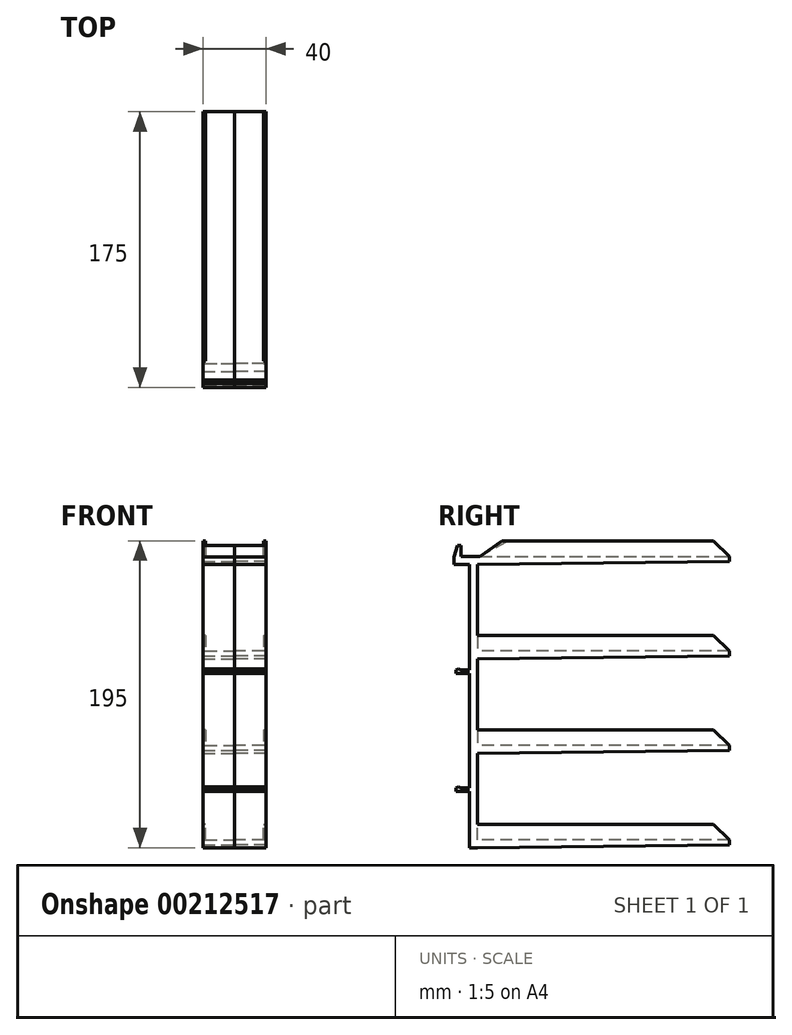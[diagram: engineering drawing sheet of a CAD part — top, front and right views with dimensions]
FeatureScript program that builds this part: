
annotation { "Feature Type Name" : "Feature", "Feature Type Description" : "" }
export const myFeature = defineFeature(function(context is Context, id is Id, definition is map)
    precondition{}
    {
        {
            var Q0;
            Q0=qCreatedBy(makeId("Right.planeOp"),FACE);
            var sketch = newSketch(context, id + "F0", { "sketchPlane" : qUnion([Q0])});
            skLineSegment(sketch, "E0", {"start": v(0, 0) * mm, "end": v(0, 67) * mm});
            skLineSegment(sketch, "E1", {"start": v(0, 67) * mm, "end": v(-10, 67) * mm});
            skLineSegment(sketch, "E2", {"start": v(-10, 67) * mm, "end": v(-10, 79) * mm});
            skLineSegment(sketch, "E3", {"start": v(-10, 79) * mm, "end": v(-5.5, 79) * mm});
            skLineSegment(sketch, "E4", {"start": v(-5.5, 79) * mm, "end": v(-5.5, 72) * mm});
            skLineSegment(sketch, "E5", {"start": v(-5.5, 72) * mm, "end": v(5, 72) * mm});
            skLineSegment(sketch, "E6", {"start": v(0, 0) * mm, "end": v(-5.5, 0) * mm});
            skLineSegment(sketch, "E7", {"start": v(-5.5, 0) * mm, "end": v(-5.5, 0.75) * mm});
            skLineSegment(sketch, "E8", {"start": v(-5.5, 0.75) * mm, "end": v(-8.5, 0.75) * mm});
            skLineSegment(sketch, "E9", {"start": v(-8.5, 0.75) * mm, "end": v(-8.5, -2.25) * mm});
            skLineSegment(sketch, "E10", {"start": v(-8.5, -2.25) * mm, "end": v(0, -2.25) * mm});
            skLineSegment(sketch, "E11", {"start": v(0, -2.25) * mm, "end": v(0, -58.03) * mm});
            skLineSegment(sketch, "E12", {"start": v(0, 0) * mm, "end": v(27.42, 0) * mm, "construction": true});
            skLineSegment(sketch, "E13", {"start": v(27.42, 0) * mm, "end": v(27.42, -75) * mm, "construction": true});
            skLineSegment(sketch, "E14", {"start": v(27.42, -75) * mm, "end": v(0, -75) * mm, "construction": true});
            skLineSegment(sketch, "E15", {"start": v(0, -58.03) * mm, "end": v(0, -75) * mm});
            skLineSegment(sketch, "E16", {"start": v(0, -75) * mm, "end": v(-5.5, -75) * mm});
            skLineSegment(sketch, "E17", {"start": v(-5.5, -75) * mm, "end": v(-5.5, -74.25) * mm});
            skLineSegment(sketch, "E18", {"start": v(-5.5, -74.25) * mm, "end": v(-8.5, -74.25) * mm});
            skLineSegment(sketch, "E19", {"start": v(-8.5, -74.25) * mm, "end": v(-8.5, -77.25) * mm});
            skLineSegment(sketch, "E20", {"start": v(-8.5, -77.25) * mm, "end": v(0, -77.25) * mm});
            skLineSegment(sketch, "E21", {"start": v(5, 72) * mm, "end": v(165, 72) * mm});
            skLineSegment(sketch, "E22", {"start": v(165, 72) * mm, "end": v(165, 69) * mm});
            skLineSegment(sketch, "E23", {"start": v(165, 72) * mm, "end": v(165, 12) * mm, "construction": true});
            skLineSegment(sketch, "E24", {"start": v(165, 12) * mm, "end": v(165, -48) * mm, "construction": true});
            skLineSegment(sketch, "E25", {"start": v(165, -48) * mm, "end": v(165, -108) * mm, "construction": true});
            skLineSegment(sketch, "E26", {"start": v(165, -108) * mm, "end": v(5, -108) * mm});
            skLineSegment(sketch, "E27", {"start": v(165, -108) * mm, "end": v(165, -111) * mm});
            skLineSegment(sketch, "E28", {"start": v(165, -111) * mm, "end": v(5, -113) * mm});
            skLineSegment(sketch, "E29", {"start": v(0, -77.25) * mm, "end": v(0, -113) * mm});
            skLineSegment(sketch, "E30", {"start": v(5, -113) * mm, "end": v(0, -113) * mm});
            skLineSegment(sketch, "E31", {"start": v(165, -48) * mm, "end": v(5, -48) * mm});
            skLineSegment(sketch, "E32", {"start": v(165, 12) * mm, "end": v(5, 12) * mm});
            skLineSegment(sketch, "E33", {"start": v(165, 12) * mm, "end": v(165, 9) * mm});
            skLineSegment(sketch, "E34", {"start": v(165, 9) * mm, "end": v(5, 7) * mm});
            skLineSegment(sketch, "E35", {"start": v(165, -48) * mm, "end": v(165, -51) * mm});
            skLineSegment(sketch, "E36", {"start": v(165, -51) * mm, "end": v(5, -53) * mm});
            skLineSegment(sketch, "E37", {"start": v(5, 72) * mm, "end": v(5, 67) * mm, "construction": true});
            skLineSegment(sketch, "E38", {"start": v(5, 67) * mm, "end": v(165, 69) * mm});
            skLineSegment(sketch, "E39", {"start": v(5, 67) * mm, "end": v(5, 12) * mm});
            skLineSegment(sketch, "E40", {"start": v(5, 7) * mm, "end": v(5, -48) * mm});
            skLineSegment(sketch, "E41", {"start": v(5, -108) * mm, "end": v(5, -53) * mm});
            skSolve(sketch);
        }
        {
            var Q0;
            Q0=makeQuery(id+"F0.imprint","IMPRINT",FACE,{"disambiguationData":[TD([[makeQuery(id+"F0.imprint","IMPRINT",EDGE,{"derivedFrom":sQuery(id+"F0.wireOp",EDGE,"E0")}),-1.0]])]});
            extrude(context, id + "F1", {"entities" : qUnion([Q0]), "depth" : 20 * mm});
        }
        {
            var Q0;
            Q0=makeQuery(id+"F1.opExtrude","CAP_FACE",FACE,{"disambiguationData":[OSD([sQuery(id+"F0.wireOp",EDGE,"E0"),sQuery(id+"F0.wireOp",EDGE,"E1"),sQuery(id+"F0.wireOp",EDGE,"E2"),sQuery(id+"F0.wireOp",EDGE,"E3"),sQuery(id+"F0.wireOp",EDGE,"E4"),sQuery(id+"F0.wireOp",EDGE,"E5"),sQuery(id+"F0.wireOp",EDGE,"E6"),sQuery(id+"F0.wireOp",EDGE,"E7"),sQuery(id+"F0.wireOp",EDGE,"E8"),sQuery(id+"F0.wireOp",EDGE,"E9"),sQuery(id+"F0.wireOp",EDGE,"E10"),sQuery(id+"F0.wireOp",EDGE,"E11"),sQuery(id+"F0.wireOp",EDGE,"E15"),sQuery(id+"F0.wireOp",EDGE,"E16"),sQuery(id+"F0.wireOp",EDGE,"E17"),sQuery(id+"F0.wireOp",EDGE,"E18"),sQuery(id+"F0.wireOp",EDGE,"E19"),sQuery(id+"F0.wireOp",EDGE,"E20"),sQuery(id+"F0.wireOp",EDGE,"E21"),sQuery(id+"F0.wireOp",EDGE,"E22"),sQuery(id+"F0.wireOp",EDGE,"E26"),sQuery(id+"F0.wireOp",EDGE,"E27"),sQuery(id+"F0.wireOp",EDGE,"E28"),sQuery(id+"F0.wireOp",EDGE,"E29"),sQuery(id+"F0.wireOp",EDGE,"E30"),sQuery(id+"F0.wireOp",EDGE,"E31"),sQuery(id+"F0.wireOp",EDGE,"E32"),sQuery(id+"F0.wireOp",EDGE,"E33"),sQuery(id+"F0.wireOp",EDGE,"E34"),sQuery(id+"F0.wireOp",EDGE,"E35"),sQuery(id+"F0.wireOp",EDGE,"E36"),sQuery(id+"F0.wireOp",EDGE,"E38"),sQuery(id+"F0.wireOp",EDGE,"E39"),sQuery(id+"F0.wireOp",EDGE,"E40"),sQuery(id+"F0.wireOp",EDGE,"E41")])],"isStart":false});
            var sketch = newSketch(context, id + "F2", { "sketchPlane" : qUnion([Q0])});
            skLineSegment(sketch, "E42", {"start": v(-7.75, 79) * mm, "end": v(-10, 71.88) * mm});
            skLineSegment(sketch, "E43", {"start": v(-10, 71.88) * mm, "end": v(-10, 79) * mm});
            skLineSegment(sketch, "E44", {"start": v(-10, 79) * mm, "end": v(-7.75, 79) * mm});
            skSolve(sketch);
        }
        {
            var Q0;
            Q0=makeQuery(id+"F2.imprint","IMPRINT",FACE,{"disambiguationData":[TD([[makeQuery(id+"F2.imprint","IMPRINT",EDGE,{"derivedFrom":sQuery(id+"F2.wireOp",EDGE,"E42")}),-1.0]])]});
            extrude(context, id + "F3", {"entities" : qUnion([Q0]), "operationType" : NewBodyOperationType.REMOVE, "endBound" : BoundingType.UP_TO_NEXT, "oppositeDirection" : true, "depth" : 10 * mm});
        }
        {
            var Q0;
            Q0=makeQuery(id+"F1.opExtrude","CAP_FACE",FACE,{"disambiguationData":[OSD([sQuery(id+"F0.wireOp",EDGE,"E0"),sQuery(id+"F0.wireOp",EDGE,"E1"),sQuery(id+"F0.wireOp",EDGE,"E2"),sQuery(id+"F0.wireOp",EDGE,"E3"),sQuery(id+"F0.wireOp",EDGE,"E4"),sQuery(id+"F0.wireOp",EDGE,"E5"),sQuery(id+"F0.wireOp",EDGE,"E6"),sQuery(id+"F0.wireOp",EDGE,"E7"),sQuery(id+"F0.wireOp",EDGE,"E8"),sQuery(id+"F0.wireOp",EDGE,"E9"),sQuery(id+"F0.wireOp",EDGE,"E10"),sQuery(id+"F0.wireOp",EDGE,"E11"),sQuery(id+"F0.wireOp",EDGE,"E15"),sQuery(id+"F0.wireOp",EDGE,"E16"),sQuery(id+"F0.wireOp",EDGE,"E17"),sQuery(id+"F0.wireOp",EDGE,"E18"),sQuery(id+"F0.wireOp",EDGE,"E19"),sQuery(id+"F0.wireOp",EDGE,"E20"),sQuery(id+"F0.wireOp",EDGE,"E21"),sQuery(id+"F0.wireOp",EDGE,"E22"),sQuery(id+"F0.wireOp",EDGE,"E26"),sQuery(id+"F0.wireOp",EDGE,"E27"),sQuery(id+"F0.wireOp",EDGE,"E28"),sQuery(id+"F0.wireOp",EDGE,"E29"),sQuery(id+"F0.wireOp",EDGE,"E30"),sQuery(id+"F0.wireOp",EDGE,"E31"),sQuery(id+"F0.wireOp",EDGE,"E32"),sQuery(id+"F0.wireOp",EDGE,"E33"),sQuery(id+"F0.wireOp",EDGE,"E34"),sQuery(id+"F0.wireOp",EDGE,"E35"),sQuery(id+"F0.wireOp",EDGE,"E36"),sQuery(id+"F0.wireOp",EDGE,"E38"),sQuery(id+"F0.wireOp",EDGE,"E39"),sQuery(id+"F0.wireOp",EDGE,"E40"),sQuery(id+"F0.wireOp",EDGE,"E41")])],"isStart":false});
            var sketch = newSketch(context, id + "F4", { "sketchPlane" : qUnion([Q0])});
            skLineSegment(sketch, "E45", {"start": v(-5.5, 0) * mm, "end": v(-7, 0.75) * mm});
            skLineSegment(sketch, "E46", {"start": v(-7, 0.75) * mm, "end": v(-8.5, 0) * mm});
            skLineSegment(sketch, "E47", {"start": v(-8.5, 0) * mm, "end": v(-8.5, 0.75) * mm});
            skLineSegment(sketch, "E48", {"start": v(-8.5, 0.75) * mm, "end": v(-7, 0.75) * mm});
            skLineSegment(sketch, "E49", {"start": v(-5.5, 0.75) * mm, "end": v(-5.5, 0) * mm});
            skSolve(sketch);
        }
        {
            var Q0;
            Q0=makeQuery(id+"F4.imprint","IMPRINT",FACE,{"disambiguationData":[TD([[makeQuery(id+"F4.imprint","IMPRINT",EDGE,{"derivedFrom":sQuery(id+"F4.wireOp",EDGE,"E46")}),-1.0]])]});
            var Q1;
            {var subQ0=sQuery(id+"F4.wireOp",EDGE,"E45");Q1=makeQuery(id+"F4.imprint","IMPRINT",FACE,{"disambiguationData":[TD([[makeQuery(id+"F4.imprint","IMPRINT",EDGE,{"derivedFrom":subQ0}),-1.0]])]});}
            extrude(context, id + "F5", {"entities" : qUnion([Q0, Q1]), "operationType" : NewBodyOperationType.REMOVE, "endBound" : BoundingType.UP_TO_NEXT, "oppositeDirection" : true, "depth" : 10 * mm});
        }
        {
            var Q0;
            Q0=makeQuery(id+"F1.opExtrude","CAP_FACE",FACE,{"disambiguationData":[OSD([sQuery(id+"F0.wireOp",EDGE,"E0"),sQuery(id+"F0.wireOp",EDGE,"E1"),sQuery(id+"F0.wireOp",EDGE,"E2"),sQuery(id+"F0.wireOp",EDGE,"E3"),sQuery(id+"F0.wireOp",EDGE,"E4"),sQuery(id+"F0.wireOp",EDGE,"E5"),sQuery(id+"F0.wireOp",EDGE,"E6"),sQuery(id+"F0.wireOp",EDGE,"E7"),sQuery(id+"F0.wireOp",EDGE,"E8"),sQuery(id+"F0.wireOp",EDGE,"E9"),sQuery(id+"F0.wireOp",EDGE,"E10"),sQuery(id+"F0.wireOp",EDGE,"E11"),sQuery(id+"F0.wireOp",EDGE,"E15"),sQuery(id+"F0.wireOp",EDGE,"E16"),sQuery(id+"F0.wireOp",EDGE,"E17"),sQuery(id+"F0.wireOp",EDGE,"E18"),sQuery(id+"F0.wireOp",EDGE,"E19"),sQuery(id+"F0.wireOp",EDGE,"E20"),sQuery(id+"F0.wireOp",EDGE,"E21"),sQuery(id+"F0.wireOp",EDGE,"E22"),sQuery(id+"F0.wireOp",EDGE,"E26"),sQuery(id+"F0.wireOp",EDGE,"E27"),sQuery(id+"F0.wireOp",EDGE,"E28"),sQuery(id+"F0.wireOp",EDGE,"E29"),sQuery(id+"F0.wireOp",EDGE,"E30"),sQuery(id+"F0.wireOp",EDGE,"E31"),sQuery(id+"F0.wireOp",EDGE,"E32"),sQuery(id+"F0.wireOp",EDGE,"E33"),sQuery(id+"F0.wireOp",EDGE,"E34"),sQuery(id+"F0.wireOp",EDGE,"E35"),sQuery(id+"F0.wireOp",EDGE,"E36"),sQuery(id+"F0.wireOp",EDGE,"E38"),sQuery(id+"F0.wireOp",EDGE,"E39"),sQuery(id+"F0.wireOp",EDGE,"E40"),sQuery(id+"F0.wireOp",EDGE,"E41")])],"isStart":false});
            var sketch = newSketch(context, id + "F6", { "sketchPlane" : qUnion([Q0])});
            skLineSegment(sketch, "E50", {"start": v(-5.5, -75) * mm, "end": v(-7, -74.25) * mm});
            skLineSegment(sketch, "E51", {"start": v(-7, -74.25) * mm, "end": v(-8.5, -75) * mm});
            skLineSegment(sketch, "E52", {"start": v(-8.5, -75) * mm, "end": v(-8.5, -74.25) * mm});
            skLineSegment(sketch, "E53", {"start": v(-8.5, -74.25) * mm, "end": v(-7, -74.25) * mm});
            skLineSegment(sketch, "E54", {"start": v(-5.5, -74.25) * mm, "end": v(-5.5, -75) * mm});
            skSolve(sketch);
        }
        {
            var Q0;
            Q0=makeQuery(id+"F6.imprint","IMPRINT",FACE,{"disambiguationData":[TD([[makeQuery(id+"F6.imprint","IMPRINT",EDGE,{"derivedFrom":sQuery(id+"F6.wireOp",EDGE,"E51")}),-1.0]])]});
            var Q1;
            {var subQ0=sQuery(id+"F6.wireOp",EDGE,"E50");Q1=makeQuery(id+"F6.imprint","IMPRINT",FACE,{"disambiguationData":[TD([[makeQuery(id+"F6.imprint","IMPRINT",EDGE,{"derivedFrom":subQ0}),-1.0]])]});}
            extrude(context, id + "F7", {"entities" : qUnion([Q0, Q1]), "operationType" : NewBodyOperationType.REMOVE, "endBound" : BoundingType.UP_TO_NEXT, "oppositeDirection" : true, "depth" : 10 * mm});
        }
        {
            var Q0;
            Q0=makeQuery(id+"F1.opExtrude","CAP_FACE",FACE,{"disambiguationData":[OSD([sQuery(id+"F0.wireOp",EDGE,"E0"),sQuery(id+"F0.wireOp",EDGE,"E1"),sQuery(id+"F0.wireOp",EDGE,"E2"),sQuery(id+"F0.wireOp",EDGE,"E3"),sQuery(id+"F0.wireOp",EDGE,"E4"),sQuery(id+"F0.wireOp",EDGE,"E5"),sQuery(id+"F0.wireOp",EDGE,"E6"),sQuery(id+"F0.wireOp",EDGE,"E7"),sQuery(id+"F0.wireOp",EDGE,"E8"),sQuery(id+"F0.wireOp",EDGE,"E9"),sQuery(id+"F0.wireOp",EDGE,"E10"),sQuery(id+"F0.wireOp",EDGE,"E11"),sQuery(id+"F0.wireOp",EDGE,"E15"),sQuery(id+"F0.wireOp",EDGE,"E16"),sQuery(id+"F0.wireOp",EDGE,"E17"),sQuery(id+"F0.wireOp",EDGE,"E18"),sQuery(id+"F0.wireOp",EDGE,"E19"),sQuery(id+"F0.wireOp",EDGE,"E20"),sQuery(id+"F0.wireOp",EDGE,"E21"),sQuery(id+"F0.wireOp",EDGE,"E22"),sQuery(id+"F0.wireOp",EDGE,"E26"),sQuery(id+"F0.wireOp",EDGE,"E27"),sQuery(id+"F0.wireOp",EDGE,"E28"),sQuery(id+"F0.wireOp",EDGE,"E29"),sQuery(id+"F0.wireOp",EDGE,"E30"),sQuery(id+"F0.wireOp",EDGE,"E31"),sQuery(id+"F0.wireOp",EDGE,"E32"),sQuery(id+"F0.wireOp",EDGE,"E33"),sQuery(id+"F0.wireOp",EDGE,"E34"),sQuery(id+"F0.wireOp",EDGE,"E35"),sQuery(id+"F0.wireOp",EDGE,"E36"),sQuery(id+"F0.wireOp",EDGE,"E38"),sQuery(id+"F0.wireOp",EDGE,"E39"),sQuery(id+"F0.wireOp",EDGE,"E40"),sQuery(id+"F0.wireOp",EDGE,"E41")])],"isStart":false});
            var sketch = newSketch(context, id + "F8", { "sketchPlane" : qUnion([Q0])});
            skLineSegment(sketch, "E55", {"start": v(165, 72) * mm, "end": v(165, 82) * mm, "construction": true});
            skLineSegment(sketch, "E56", {"start": v(165, 82) * mm, "end": v(155, 82) * mm, "construction": true});
            skLineSegment(sketch, "E57", {"start": v(165, 12) * mm, "end": v(165, 22) * mm, "construction": true});
            skLineSegment(sketch, "E58", {"start": v(165, 22) * mm, "end": v(155, 22) * mm, "construction": true});
            skLineSegment(sketch, "E59", {"start": v(165, -48) * mm, "end": v(165, -38) * mm, "construction": true});
            skLineSegment(sketch, "E60", {"start": v(165, -38) * mm, "end": v(155, -38) * mm, "construction": true});
            skLineSegment(sketch, "E61", {"start": v(165, -108) * mm, "end": v(164.88, -98) * mm, "construction": true});
            skLineSegment(sketch, "E62", {"start": v(164.88, -98) * mm, "end": v(154.88, -98.13) * mm, "construction": true});
            skLineSegment(sketch, "E63", {"start": v(165, 72) * mm, "end": v(155, 82) * mm});
            skLineSegment(sketch, "E64", {"start": v(6.64, 82) * mm, "end": v(6.64, 72) * mm});
            skLineSegment(sketch, "E65", {"start": v(6.64, 72) * mm, "end": v(165, 72) * mm});
            skLineSegment(sketch, "E66", {"start": v(155, 82) * mm, "end": v(6.64, 82) * mm});
            skLineSegment(sketch, "E67", {"start": v(165, 12) * mm, "end": v(155, 22) * mm});
            skLineSegment(sketch, "E68", {"start": v(5, 22) * mm, "end": v(5, 12) * mm});
            skLineSegment(sketch, "E69", {"start": v(5, 12) * mm, "end": v(165, 12) * mm});
            skLineSegment(sketch, "E70", {"start": v(155, 22) * mm, "end": v(5, 22) * mm});
            skLineSegment(sketch, "E71", {"start": v(165, -48) * mm, "end": v(155, -38) * mm});
            skLineSegment(sketch, "E72", {"start": v(5, -38) * mm, "end": v(155, -38) * mm});
            skLineSegment(sketch, "E73", {"start": v(5, -38) * mm, "end": v(5, -48) * mm});
            skLineSegment(sketch, "E74", {"start": v(5, -48) * mm, "end": v(165, -48) * mm});
            skLineSegment(sketch, "E75", {"start": v(154.88, -98.13) * mm, "end": v(5, -98.13) * mm});
            skLineSegment(sketch, "E76", {"start": v(5, -98.13) * mm, "end": v(5, -108) * mm});
            skLineSegment(sketch, "E77", {"start": v(5, -108) * mm, "end": v(165, -108) * mm});
            skLineSegment(sketch, "E78", {"start": v(165, -108) * mm, "end": v(154.88, -98.13) * mm});
            skSolve(sketch);
        }
        {
            var Q0;
            Q0=makeQuery(id+"F8.imprint","IMPRINT",FACE,{"disambiguationData":[TD([[makeQuery(id+"F8.imprint","IMPRINT",EDGE,{"derivedFrom":sQuery(id+"F8.wireOp",EDGE,"E63")}),1.0]])]});
            var Q1;
            Q1=makeQuery(id+"F8.imprint","IMPRINT",FACE,{"disambiguationData":[TD([[makeQuery(id+"F8.imprint","IMPRINT",EDGE,{"derivedFrom":sQuery(id+"F8.wireOp",EDGE,"E67")}),1.0]])]});
            var Q2;
            Q2=makeQuery(id+"F8.imprint","IMPRINT",FACE,{"disambiguationData":[TD([[makeQuery(id+"F8.imprint","IMPRINT",EDGE,{"derivedFrom":sQuery(id+"F8.wireOp",EDGE,"E71")}),1.0]])]});
            var Q3;
            Q3=makeQuery(id+"F8.imprint","IMPRINT",FACE,{"disambiguationData":[TD([[makeQuery(id+"F8.imprint","IMPRINT",EDGE,{"derivedFrom":sQuery(id+"F8.wireOp",EDGE,"E75")}),1.0]])]});
            extrude(context, id + "F9", {"entities" : qUnion([Q0, Q1, Q2, Q3]), "operationType" : NewBodyOperationType.ADD, "oppositeDirection" : true, "depth" : 1.5 * mm});
        }
        {
            var Q0;
            Q0=makeQuery(id+"F1.opExtrude","SWEPT_BODY",BODY,{"disambiguationData":[OSD([sQuery(id+"F0.wireOp",EDGE,"E0"),sQuery(id+"F0.wireOp",EDGE,"E1"),sQuery(id+"F0.wireOp",EDGE,"E2"),sQuery(id+"F0.wireOp",EDGE,"E3"),sQuery(id+"F0.wireOp",EDGE,"E4"),sQuery(id+"F0.wireOp",EDGE,"E5"),sQuery(id+"F0.wireOp",EDGE,"E6"),sQuery(id+"F0.wireOp",EDGE,"E7"),sQuery(id+"F0.wireOp",EDGE,"E8"),sQuery(id+"F0.wireOp",EDGE,"E9"),sQuery(id+"F0.wireOp",EDGE,"E10"),sQuery(id+"F0.wireOp",EDGE,"E11"),sQuery(id+"F0.wireOp",EDGE,"E15"),sQuery(id+"F0.wireOp",EDGE,"E16"),sQuery(id+"F0.wireOp",EDGE,"E17"),sQuery(id+"F0.wireOp",EDGE,"E18"),sQuery(id+"F0.wireOp",EDGE,"E19"),sQuery(id+"F0.wireOp",EDGE,"E20"),sQuery(id+"F0.wireOp",EDGE,"E21"),sQuery(id+"F0.wireOp",EDGE,"E22"),sQuery(id+"F0.wireOp",EDGE,"E26"),sQuery(id+"F0.wireOp",EDGE,"E27"),sQuery(id+"F0.wireOp",EDGE,"E28"),sQuery(id+"F0.wireOp",EDGE,"E29"),sQuery(id+"F0.wireOp",EDGE,"E30"),sQuery(id+"F0.wireOp",EDGE,"E31"),sQuery(id+"F0.wireOp",EDGE,"E32"),sQuery(id+"F0.wireOp",EDGE,"E33"),sQuery(id+"F0.wireOp",EDGE,"E34"),sQuery(id+"F0.wireOp",EDGE,"E35"),sQuery(id+"F0.wireOp",EDGE,"E36"),sQuery(id+"F0.wireOp",EDGE,"E38"),sQuery(id+"F0.wireOp",EDGE,"E39"),sQuery(id+"F0.wireOp",EDGE,"E40"),sQuery(id+"F0.wireOp",EDGE,"E41")])]});
            var Q1;
            Q1=qCreatedBy(makeId("Right.planeOp"),FACE);
            mirror(context, id + "F10", {"entities" : qUnion([Q0]), "mirrorPlane" : qUnion([Q1])});
        }
        {
            var Q0;
            Q0=makeQuery(id+"F9.boolean.opBoolean","MERGE",FACE,{"derivedFrom":[makeQuery(id+"F1.opExtrude","CAP_FACE",FACE,{"disambiguationData":[OSD([sQuery(id+"F0.wireOp",EDGE,"E0"),sQuery(id+"F0.wireOp",EDGE,"E1"),sQuery(id+"F0.wireOp",EDGE,"E2"),sQuery(id+"F0.wireOp",EDGE,"E3"),sQuery(id+"F0.wireOp",EDGE,"E4"),sQuery(id+"F0.wireOp",EDGE,"E5"),sQuery(id+"F0.wireOp",EDGE,"E6"),sQuery(id+"F0.wireOp",EDGE,"E7"),sQuery(id+"F0.wireOp",EDGE,"E8"),sQuery(id+"F0.wireOp",EDGE,"E9"),sQuery(id+"F0.wireOp",EDGE,"E10"),sQuery(id+"F0.wireOp",EDGE,"E11"),sQuery(id+"F0.wireOp",EDGE,"E15"),sQuery(id+"F0.wireOp",EDGE,"E16"),sQuery(id+"F0.wireOp",EDGE,"E17"),sQuery(id+"F0.wireOp",EDGE,"E18"),sQuery(id+"F0.wireOp",EDGE,"E19"),sQuery(id+"F0.wireOp",EDGE,"E20"),sQuery(id+"F0.wireOp",EDGE,"E21"),sQuery(id+"F0.wireOp",EDGE,"E22"),sQuery(id+"F0.wireOp",EDGE,"E26"),sQuery(id+"F0.wireOp",EDGE,"E27"),sQuery(id+"F0.wireOp",EDGE,"E28"),sQuery(id+"F0.wireOp",EDGE,"E29"),sQuery(id+"F0.wireOp",EDGE,"E30"),sQuery(id+"F0.wireOp",EDGE,"E31"),sQuery(id+"F0.wireOp",EDGE,"E32"),sQuery(id+"F0.wireOp",EDGE,"E33"),sQuery(id+"F0.wireOp",EDGE,"E34"),sQuery(id+"F0.wireOp",EDGE,"E35"),sQuery(id+"F0.wireOp",EDGE,"E36"),sQuery(id+"F0.wireOp",EDGE,"E38"),sQuery(id+"F0.wireOp",EDGE,"E39"),sQuery(id+"F0.wireOp",EDGE,"E40"),sQuery(id+"F0.wireOp",EDGE,"E41")])],"isStart":false}),makeQuery(id+"F9.opExtrude","CAP_FACE",FACE,{"disambiguationData":[OSD([sQuery(id+"F8.wireOp",EDGE,"E63"),sQuery(id+"F8.wireOp",EDGE,"E64"),sQuery(id+"F8.wireOp",EDGE,"E65"),sQuery(id+"F8.wireOp",EDGE,"E66")])],"isStart":true}),makeQuery(id+"F9.opExtrude","CAP_FACE",FACE,{"disambiguationData":[OSD([sQuery(id+"F8.wireOp",EDGE,"E67"),sQuery(id+"F8.wireOp",EDGE,"E68"),sQuery(id+"F8.wireOp",EDGE,"E69"),sQuery(id+"F8.wireOp",EDGE,"E70")])],"isStart":true}),makeQuery(id+"F9.opExtrude","CAP_FACE",FACE,{"disambiguationData":[OSD([sQuery(id+"F8.wireOp",EDGE,"E71"),sQuery(id+"F8.wireOp",EDGE,"E72"),sQuery(id+"F8.wireOp",EDGE,"E73"),sQuery(id+"F8.wireOp",EDGE,"E74")])],"isStart":true}),makeQuery(id+"F9.opExtrude","CAP_FACE",FACE,{"disambiguationData":[OSD([sQuery(id+"F8.wireOp",EDGE,"E75"),sQuery(id+"F8.wireOp",EDGE,"E76"),sQuery(id+"F8.wireOp",EDGE,"E77"),sQuery(id+"F8.wireOp",EDGE,"E78")])],"isStart":true})]});
            var sketch = newSketch(context, id + "F11", { "sketchPlane" : qUnion([Q0])});
            skLineSegment(sketch, "E79", {"start": v(6.64, 72) * mm, "end": v(20.55, 82) * mm});
            skLineSegment(sketch, "E80", {"start": v(20.55, 82) * mm, "end": v(6.64, 82) * mm});
            skLineSegment(sketch, "E81", {"start": v(6.64, 82) * mm, "end": v(6.64, 72) * mm});
            skSolve(sketch);
        }
        {
            var Q0;
            Q0=makeQuery(id+"F11.imprint","IMPRINT",FACE,{"disambiguationData":[TD([[makeQuery(id+"F11.imprint","IMPRINT",EDGE,{"derivedFrom":sQuery(id+"F11.wireOp",EDGE,"E79")}),1.0]])]});
            extrude(context, id + "F12", {"entities" : qUnion([Q0]), "operationType" : NewBodyOperationType.REMOVE, "endBound" : BoundingType.UP_TO_NEXT, "oppositeDirection" : true, "depth" : 25 * mm});
        }
        {
            var Q0;
            Q0=makeQuery(id+"F10.opPattern","COPY",FACE,{"derivedFrom":makeQuery(id+"F9.boolean.opBoolean","MERGE",FACE,{"derivedFrom":[makeQuery(id+"F1.opExtrude","CAP_FACE",FACE,{"disambiguationData":[OSD([sQuery(id+"F0.wireOp",EDGE,"E0"),sQuery(id+"F0.wireOp",EDGE,"E1"),sQuery(id+"F0.wireOp",EDGE,"E2"),sQuery(id+"F0.wireOp",EDGE,"E3"),sQuery(id+"F0.wireOp",EDGE,"E4"),sQuery(id+"F0.wireOp",EDGE,"E5"),sQuery(id+"F0.wireOp",EDGE,"E6"),sQuery(id+"F0.wireOp",EDGE,"E7"),sQuery(id+"F0.wireOp",EDGE,"E8"),sQuery(id+"F0.wireOp",EDGE,"E9"),sQuery(id+"F0.wireOp",EDGE,"E10"),sQuery(id+"F0.wireOp",EDGE,"E11"),sQuery(id+"F0.wireOp",EDGE,"E15"),sQuery(id+"F0.wireOp",EDGE,"E16"),sQuery(id+"F0.wireOp",EDGE,"E17"),sQuery(id+"F0.wireOp",EDGE,"E18"),sQuery(id+"F0.wireOp",EDGE,"E19"),sQuery(id+"F0.wireOp",EDGE,"E20"),sQuery(id+"F0.wireOp",EDGE,"E21"),sQuery(id+"F0.wireOp",EDGE,"E22"),sQuery(id+"F0.wireOp",EDGE,"E26"),sQuery(id+"F0.wireOp",EDGE,"E27"),sQuery(id+"F0.wireOp",EDGE,"E28"),sQuery(id+"F0.wireOp",EDGE,"E29"),sQuery(id+"F0.wireOp",EDGE,"E30"),sQuery(id+"F0.wireOp",EDGE,"E31"),sQuery(id+"F0.wireOp",EDGE,"E32"),sQuery(id+"F0.wireOp",EDGE,"E33"),sQuery(id+"F0.wireOp",EDGE,"E34"),sQuery(id+"F0.wireOp",EDGE,"E35"),sQuery(id+"F0.wireOp",EDGE,"E36"),sQuery(id+"F0.wireOp",EDGE,"E38"),sQuery(id+"F0.wireOp",EDGE,"E39"),sQuery(id+"F0.wireOp",EDGE,"E40"),sQuery(id+"F0.wireOp",EDGE,"E41")])],"isStart":false}),makeQuery(id+"F9.opExtrude","CAP_FACE",FACE,{"disambiguationData":[OSD([sQuery(id+"F8.wireOp",EDGE,"E63"),sQuery(id+"F8.wireOp",EDGE,"E64"),sQuery(id+"F8.wireOp",EDGE,"E65"),sQuery(id+"F8.wireOp",EDGE,"E66")])],"isStart":true}),makeQuery(id+"F9.opExtrude","CAP_FACE",FACE,{"disambiguationData":[OSD([sQuery(id+"F8.wireOp",EDGE,"E67"),sQuery(id+"F8.wireOp",EDGE,"E68"),sQuery(id+"F8.wireOp",EDGE,"E69"),sQuery(id+"F8.wireOp",EDGE,"E70")])],"isStart":true}),makeQuery(id+"F9.opExtrude","CAP_FACE",FACE,{"disambiguationData":[OSD([sQuery(id+"F8.wireOp",EDGE,"E71"),sQuery(id+"F8.wireOp",EDGE,"E72"),sQuery(id+"F8.wireOp",EDGE,"E73"),sQuery(id+"F8.wireOp",EDGE,"E74")])],"isStart":true}),makeQuery(id+"F9.opExtrude","CAP_FACE",FACE,{"disambiguationData":[OSD([sQuery(id+"F8.wireOp",EDGE,"E75"),sQuery(id+"F8.wireOp",EDGE,"E76"),sQuery(id+"F8.wireOp",EDGE,"E77"),sQuery(id+"F8.wireOp",EDGE,"E78")])],"isStart":true})]}),"instanceName":"1"});
            var sketch = newSketch(context, id + "F13", { "sketchPlane" : qUnion([Q0])});
            skLineSegment(sketch, "E82", {"start": v(-6.64, 72) * mm, "end": v(-24.3, 82) * mm});
            skLineSegment(sketch, "E83", {"start": v(-24.3, 82) * mm, "end": v(-6.64, 82) * mm});
            skLineSegment(sketch, "E84", {"start": v(-6.64, 82) * mm, "end": v(-6.64, 72) * mm});
            skSolve(sketch);
        }
        {
            var Q0;
            Q0=makeQuery(id+"F13.imprint","IMPRINT",FACE,{"disambiguationData":[TD([[makeQuery(id+"F13.imprint","IMPRINT",EDGE,{"derivedFrom":sQuery(id+"F13.wireOp",EDGE,"E82")}),-1.0]])]});
            extrude(context, id + "F14", {"entities" : qUnion([Q0]), "operationType" : NewBodyOperationType.REMOVE, "endBound" : BoundingType.UP_TO_NEXT, "oppositeDirection" : true, "depth" : 25 * mm});
        }
    });
